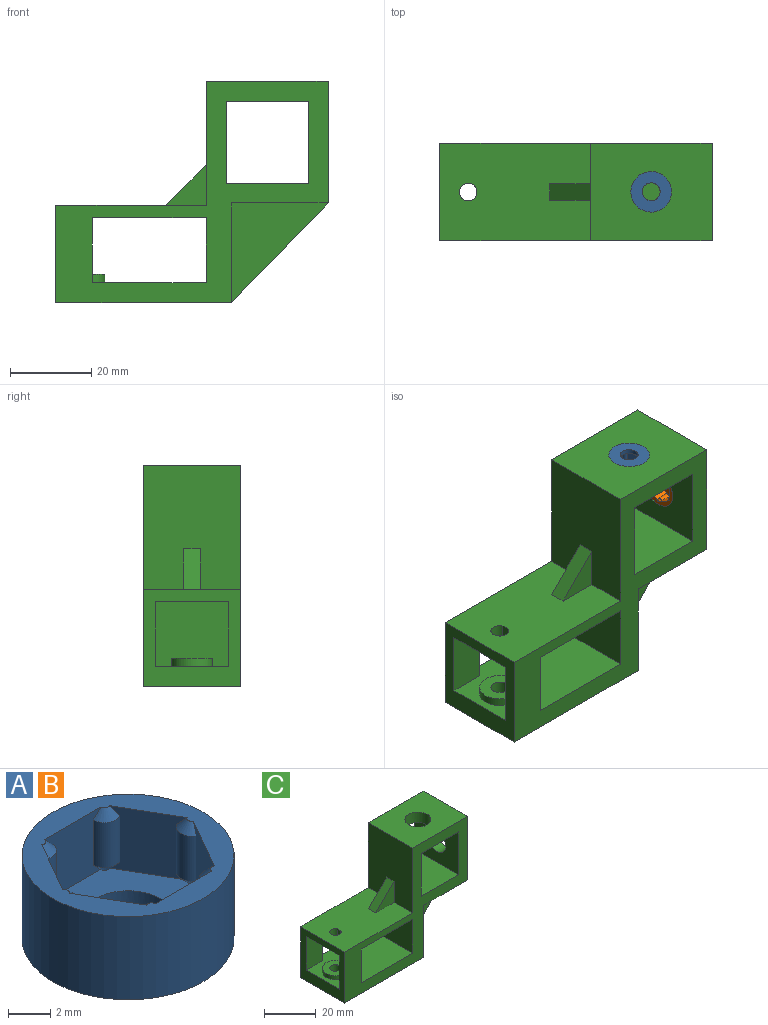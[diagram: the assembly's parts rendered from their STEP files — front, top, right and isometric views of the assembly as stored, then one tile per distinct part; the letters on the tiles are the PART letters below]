
ASSEMBLY  parts=3 mates=2
PART A: 29 faces, bbox 10x10x4.8 mm
  f0: plane 3.77x3.6mm, normal (0,-1,0), area 10.5mm2, adj f7,f8,f9,f10,f17,f18,f19,f26
  f1: plane 3.6x3.27mm, normal (-0.87,-0.5,0), area 10.5mm2, adj f7,f8,f9,f10,f14,f15,f16,f26
  f2: plane 3.6x3.27mm, normal (-0.87,0.5,0), area 10.5mm2, adj f7,f11,f12,f13,f14,f15,f16,f26
  f3: plane 3.77x3.6mm, normal (0,1,0), area 10.5mm2, adj f7,f11,f12,f13,f23,f24,f25,f26
  f4: plane 3.6x3.27mm, normal (0.87,0.5,0), area 10.5mm2, adj f7,f20,f21,f22,f23,f24,f25,f26
  f5: cylinder r=5mm len=10mm, axis (0,0,-1), area 150.8mm2, adj f7,f27
  f6: plane 3.6x3.27mm, normal (0.87,-0.5,0), area 10.5mm2, adj f7,f17,f18,f19,f20,f21,f22,f26
  f7: plane 10x10mm, normal (0,0,1), area 31.5mm2, adj f0,f1,f2,f3,f4,f5,f6,f9
  f8: cylinder r=0.75mm len=2.6mm, axis (0,0,-1), area 4.1mm2, adj f0,f1,f9,f10
  f9: cone r=0.25mm half-angle=45deg, axis (0,0,-1), area 0.7mm2, adj f0,f1,f7,f8
  f10: cone r=0.75mm half-angle=45deg, axis (0,0,1), area 0.7mm2, adj f0,f1,f8,f26
  f11: cylinder r=0.75mm len=2.6mm, axis (0,0,-1), area 4.1mm2, adj f2,f3,f12,f13
  f12: cone r=0.25mm half-angle=45deg, axis (0,0,-1), area 0.7mm2, adj f2,f3,f7,f11
  f13: cone r=0.75mm half-angle=45deg, axis (0,0,1), area 0.7mm2, adj f2,f3,f11,f26
  f14: cylinder r=0.75mm len=2.6mm, axis (0,0,-1), area 4.1mm2, adj f1,f2,f15,f16
  f15: cone r=0.25mm half-angle=45deg, axis (0,0,-1), area 0.7mm2, adj f1,f2,f7,f14
  f16: cone r=0.75mm half-angle=45deg, axis (0,0,1), area 0.7mm2, adj f1,f2,f14,f26
  f17: cone r=0.75mm half-angle=45deg, axis (0,0,1), area 0.7mm2, adj f0,f6,f19,f26
  f18: cone r=0.25mm half-angle=45deg, axis (0,0,-1), area 0.7mm2, adj f0,f6,f7,f19
  f19: cylinder r=0.75mm len=2.6mm, axis (0,0,-1), area 4.1mm2, adj f0,f6,f17,f18
  f20: cone r=0.75mm half-angle=45deg, axis (0,0,1), area 0.7mm2, adj f4,f6,f22,f26
  f21: cone r=0.25mm half-angle=45deg, axis (0,0,-1), area 0.7mm2, adj f4,f6,f7,f22
  f22: cylinder r=0.75mm len=2.6mm, axis (0,0,-1), area 4.1mm2, adj f4,f6,f20,f21
  f23: cylinder r=0.75mm len=2.6mm, axis (0,0,-1), area 4.1mm2, adj f3,f4,f24,f25
  f24: cone r=0.25mm half-angle=45deg, axis (0,0,-1), area 0.7mm2, adj f3,f4,f7,f23
  f25: cone r=0.75mm half-angle=45deg, axis (0,0,1), area 0.7mm2, adj f3,f4,f23,f26
  f26: plane 8.29x7.4mm, normal (0,0,1), area 31.8mm2, adj f0,f1,f2,f3,f4,f6,f10,f13
  f27: plane 10x10mm, normal (0,0,-1), area 63.3mm2, adj f5,f28
  f28: cylinder r=2.2mm len=4.4mm, axis (0,0,-1), area 16.6mm2, adj f26,f27
PART B: same geometry as A
PART C: 36 faces, bbox 67x24x54.6 mm
  f0: plane 30.6x24mm, normal (-1,0,0), area 694.4mm2, adj f4,f5,f6,f20,f21,f22,f33
  f1: plane 24x16mm, normal (-1,0,0), area 384mm2, adj f4,f5,f23,f30
  f2: plane 23.84x10mm, normal (0,0,-1), area 238.4mm2, adj f5,f8,f16,f18
  f3: plane 24.6x10mm, normal (1,0,0), area 246mm2, adj f4,f7,f15,f19
  f4: plane 67x54.6mm, normal (0,1,0), area 1083.4mm2, adj f0,f1,f3,f6,f7,f8,f9,f10
  f5: plane 67x54.6mm, normal (0,-1,0), area 1083.4mm2, adj f0,f1,f2,f6,f8,f9,f10,f11
  f6: plane 30x24mm, normal (0,0,1), area 641.5mm2, adj f0,f4,f5,f8,f13
  f7: plane 23.84x10mm, normal (0,0,-1), area 238.4mm2, adj f3,f4,f8,f19
  f8: plane 30x24mm, normal (1,0,0), area 641.5mm2, adj f2,f4,f5,f6,f7,f14,f17
  f9: plane 24x20.2mm, normal (0,0,-1), area 406.3mm2, adj f4,f5,f10,f12,f13
  f10: plane 24x20.2mm, normal (-1,0,0), area 406.3mm2, adj f4,f5,f9,f11,f14
  f11: plane 24x20.2mm, normal (0,0,1), area 484.8mm2, adj f4,f5,f10,f12
  f12: plane 24x20.2mm, normal (1,0,0), area 484.8mm2, adj f4,f5,f9,f11
  f13: cylinder r=5mm len=10mm, axis (0,0,1), area 153.9mm2, adj f6,f9
  f14: cylinder r=5mm len=10mm, axis (1,0,0), area 153.9mm2, adj f8,f10
  f15: plane 43.16x24mm, normal (0,0,-1), area 1020.6mm2, adj f3,f4,f5,f16,f17,f26,f27
  f16: plane 24.6x10mm, normal (1,0,0), area 246mm2, adj f2,f5,f15,f18
  f17: plane 24.6x23.84mm, normal (0.72,0,-0.7), area 137mm2, adj f8,f15,f18,f19
  f18: plane 24.6x23.84mm, normal (0,-1,0), area 293.3mm2, adj f2,f16,f17
  f19: plane 24.6x23.84mm, normal (0,1,0), area 293.3mm2, adj f3,f7,f17
  f20: plane 10x10mm, normal (-0.71,0,0.71), area 56.6mm2, adj f0,f21,f22,f33
  f21: plane 10x10mm, normal (0,-1,0), area 50mm2, adj f0,f20,f33
  f22: plane 10x10mm, normal (0,1,0), area 50mm2, adj f0,f20,f33
  f23: plane 37x24mm, normal (0,0,1), area 755.5mm2, adj f1,f4,f5,f24,f26,f28,f29,f31
  f24: cylinder r=5mm len=10mm, axis (0,0,1), area 62.8mm2, adj f23,f25
  f25: plane 10x10mm, normal (0,0,1), area 63.3mm2, adj f24,f27
  f26: plane 24x24mm, normal (-1,0,0), area 288mm2, adj f4,f5,f15,f23,f28,f30,f31,f33
  f27: cylinder r=2.2mm len=7mm, axis (0,0,1), area 96.8mm2, adj f15,f25
  f28: plane 16x9mm, normal (0,-1,0), area 144mm2, adj f23,f26,f29,f30
  f29: plane 16x3mm, normal (1,0,0), area 48mm2, adj f4,f23,f28,f30
  f30: plane 37x24mm, normal (0,0,-1), area 819mm2, adj f1,f4,f5,f26,f28,f29,f31,f32
  f31: plane 16x9mm, normal (0,1,0), area 144mm2, adj f23,f26,f30,f32
  f32: plane 16x3mm, normal (1,0,0), area 48mm2, adj f5,f23,f30,f31
  f33: plane 37x24mm, normal (0,0,1), area 833mm2, adj f0,f4,f5,f20,f21,f22,f26,f34
  f34: cylinder r=2.2mm len=4.4mm, axis (0,0,1), area 35.8mm2, adj f30,f33,f35
  f35: plane 3x1.83mm, normal (-1,0,0), area 5.5mm2, adj f30,f33,f34
PLACE A rot(axis=(1,0,0),180deg) t=(15,0,13.8)mm
PLACE B rot(axis=(0,-1,0),90deg) t=(28.8,0,0)mm
PLACE C at identity
MATE fastened A.f5 <-> C.f13  axis (0,0,1) through (15,0,15)mm
MATE fastened B.f5 <-> C.f14  axis (1,0,0) through (30,0,0)mm
